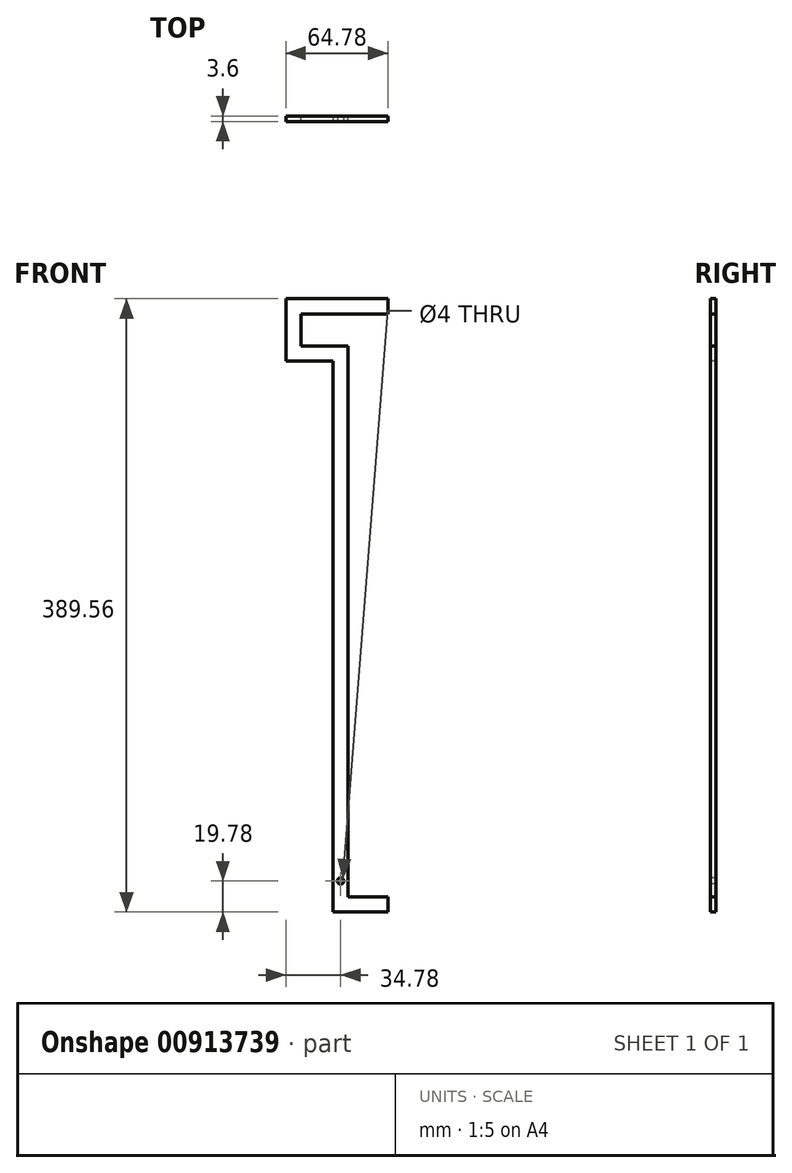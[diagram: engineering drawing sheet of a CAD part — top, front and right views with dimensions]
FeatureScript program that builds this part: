
annotation { "Feature Type Name" : "Feature", "Feature Type Description" : "" }
export const myFeature = defineFeature(function(context is Context, id is Id, definition is map)
    precondition{}
    {
        {
            var Q0;
            Q0=qCreatedBy(makeId("Front.planeOp"),FACE);
            var sketch = newSketch(context, id + "F0", { "sketchPlane" : qUnion([Q0])});
            skLineSegment(sketch, "E0", {"start": v(30, -15) * mm, "end": v(0, -15) * mm});
            skLineSegment(sketch, "E1", {"start": v(0, -15) * mm, "end": v(0, 335) * mm});
            skLineSegment(sketch, "E2", {"start": v(0, 335) * mm, "end": v(-30, 335) * mm});
            skLineSegment(sketch, "E3", {"start": v(-30, 335) * mm, "end": v(-30, 365) * mm});
            skLineSegment(sketch, "E4", {"start": v(-30, 365) * mm, "end": v(30, 365) * mm});
            skSolve(sketch);
        }
        {
            var Q0;
            Q0=qCreatedBy(makeId("Right.planeOp"),FACE);
            var sketch = newSketch(context, id + "F1", { "sketchPlane" : qUnion([Q0])});
            skLineSegment(sketch, "E5.bottom", {"start": v(1.8, -19.78) * mm, "end": v(-1.8, -19.78) * mm});
            skLineSegment(sketch, "E5.top", {"start": v(1.8, -10.22) * mm, "end": v(-1.8, -10.22) * mm});
            skLineSegment(sketch, "E5.left", {"start": v(1.8, -19.78) * mm, "end": v(1.8, -10.22) * mm});
            skLineSegment(sketch, "E5.right", {"start": v(-1.8, -19.78) * mm, "end": v(-1.8, -10.22) * mm});
            skPoint(sketch, "E5.middle", {"position": v(0, -15) * mm});
            skPoint(sketch, "E6.middle", {"position": v(0, -10.22) * mm});
            skSolve(sketch);
        }
        {
            var Q0;
            Q0=makeQuery(id+"F1.imprint","IMPRINT",FACE,{"disambiguationData":[TD([[makeQuery(id+"F1.imprint","IMPRINT",EDGE,{"derivedFrom":sQuery(id+"F1.wireOp",EDGE,"E5.bottom")}),-1.0]])]});
            var Q1;
            Q1=sQuery(id+"F0.wireOp",EDGE,"E0");
            var Q2;
            Q2=sQuery(id+"F0.wireOp",EDGE,"E1");
            var Q3;
            Q3=sQuery(id+"F0.wireOp",EDGE,"E2");
            var Q4;
            Q4=sQuery(id+"F0.wireOp",EDGE,"E3");
            var Q5;
            Q5=sQuery(id+"F0.wireOp",EDGE,"E4");
            sweep(context, id + "F2", {"profiles" : qUnion([Q0]), "path" : qUnion([Q1, Q2, Q3, Q4, Q5])});
        }
        {
            var Q0;
            Q0=makeQuery(id+"F2.opSweep","SWEPT_FACE",FACE,{"disambiguationData":[OSD([sQuery(id+"F0.wireOp",EDGE,"E4"),sQuery(id+"F1.wireOp",EDGE,"E5.right")])]});
            var sketch = newSketch(context, id + "F3", { "sketchPlane" : qUnion([Q0])});
            skCircle(sketch, "E7", {"center": v(0, 0) * mm, "radius": 1.76 * mm});
            skSolve(sketch);
        }
        {
            var Q0;
            Q0=sQuery(id+"F3.wireOp",VERTEX,"E7.center");
            var Q1;
            Q1=makeQuery(id+"F2.opSweep","SWEPT_BODY",BODY,{"disambiguationData":[OSD([sQuery(id+"F0.wireOp",EDGE,"E4"),sQuery(id+"F1.wireOp",EDGE,"E5.bottom"),sQuery(id+"F1.wireOp",EDGE,"E5.top"),sQuery(id+"F1.wireOp",EDGE,"E5.left"),sQuery(id+"F1.wireOp",EDGE,"E5.right")])]});
            hole(context, id + "F4", {"style" : HoleStyle.SIMPLE, "endStyle" : HoleEndStyle.BLIND, "holeDiameter" : 4 * mm, "majorDiameter" : 5 * mm, "holeDepth" : 12 * mm, "isTappedThrough" : true, "tappedDepth" : 12 * mm, "tapClearance" : 3, "locations" : qUnion([Q0]), "scope" : qUnion([Q1])});
        }
    });
